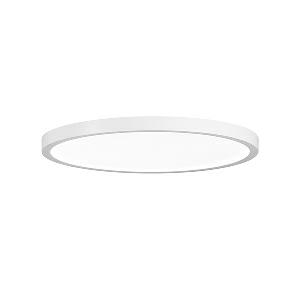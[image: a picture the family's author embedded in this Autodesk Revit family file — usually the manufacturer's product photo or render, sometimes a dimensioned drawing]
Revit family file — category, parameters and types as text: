
# Revit family: vivaa_fit_-_via_6000_940_d_00813052_e147
name_source: partatom
category: Lighting Fixtures
units: mm (PartAtom-declared; Revit-internal decimal feet)

## family parameters
Cut with Voids When Loaded = No
Host = Face
Light Source = No
Part Type = Normal
Room Calculation Point = No
Round Connector Dimension = Use Diameter
Shared = No

## types (1)
- VIVAA.fit - VIA 6000/940/D (1 x LED, 6400 lm, 4000K)
    Apparent Load = 53 VA
    Approval mark = CE
    CIE Flux Codes = 66 90 98 45 100
    Color Rendering = 90-100
    Color Temperature = 4000K
    Control Gear = Electronic ballast
    Default Elevation = 1800 mm
    Description = VIA 6000/940/D|Surface-mounted luminaire.|light source:   Cold white   |work equipment: Power supply unit|luminous flux: 6400 lm|light distribution: Direct/indirect|class of protection: I|mains lead: Direct power supply 5 pin|glare control: optical film|special features: DALI Load 2x, Suitable as emergency lighting, Separated, direct and indirect light individually adjustable|
    Frequency = 50 Hz, 60 Hz
    Height = 48 mm  [stored 0.15748 ft]
    Lamp = 1 x LED
    Lamp Light Flux = 6400 lm
    Lamp count = 1
    Length = 450 mm
    Luminous efficacy = 121 lm/W
    Manufacturer = Waldmann
    ModVariant = No
    Model = 00813052
    Mounting Place = Ceiling
    Mounting Type = Surface mounted
    Number of Poles = 1
    OnlyDefault = Yes
    Power Factor = 1
    Product Name = VIVAA.fit - VIA 6000/940/D
    Product group = Ceiling mounted luminaire
    ProductGroupID = 3
    Protection Class = Protection class I
    Protection Degree = Degree of protection
    RLX_Detail_Level = 1
    RLX_Emergency_Light_Flux = 0 lm
    RLX_Emergency_Type = 0
    RLX_Emergency_Type_DB = No
    RlxData = <blob elided: 20481 chars, md5=0f4ca58b>
    Socket = socket
    Standby Power = 0 W
    System Light Flux = 6400 lm
    System Power = 53 W
    Type Comments = Product without accessories
    Type Image = vivaa_2.0_anbau_450mm.jpg
    URL = http://relux.com
    VarID = ---
    Voltage = 230 V
    Voltage Range = 220-240 V
    Weight = 0.00 kg
    Width = 0 mm  [stored 0 ft]

note: [stored X ft] marks values corroborated as IEEE doubles in the binary element streams (Revit-internal decimal feet)

## geometry (parser evidence)
native form markers: Blend x4, Sweep x13
no freeform markers — native parametric forms only
